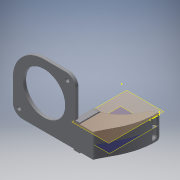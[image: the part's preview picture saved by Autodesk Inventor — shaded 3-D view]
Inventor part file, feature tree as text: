
AUTODESK INVENTOR PART (.ipt)
format: ipt  version: 2016 (Build 200138000, 138)  size: 1,453,568 bytes
history: native  units: mm
features: projected_geometry x29, sketch x27, extrude x24, fillet x11, reference x5, plane x2, chamfer x2, shell x1, imported_body x1, boolean_combine x1
ambient origin geometry x8: Origin, YZ Plane, XZ Plane, XY Plane, X Axis, Y Axis, Z Axis, Center Point
bodies: Solid1 (feature_tree), Solid2 (feature_tree)
feature tree (103):
  plane  "Work Plane1"
  extrude  "Extrusion1"  Depth=25.0mm TaperAngle=45.0deg
  chamfer  "Chamfer1"  Distance=2.0mm
  sketch  "Sketch2"  dims[d5=2.0mm]
  shell  "Shell1"  Thickness=3.0mm
  extrude  "Extrusion2"  Depth=2.0mm
  sketch  "Sketch4"  dims[d10=5.5mm d11=2.0mm d12=17.25mm d13=4.0mm d14=16.0mm d15=0.0mm d21=1.0mm d22=0.0mm]
  sketch  "Sketch5"  dims[d23=11.0mm d24=1.0mm d25=45.0deg d26=0.5mm d27=0.0mm]
  fillet  "Fillet1"  Radius=17.25mm
  fillet  "Fillet2"  Radius=4.0mm
  fillet  "Fillet3"  Radius=16.0mm
  fillet  "Fillet4"  Radius=1.0mm
  fillet  "Fillet5"  Radius=0.5mm
  extrude  "Extrusion3"  Depth=3.0mm TaperAngle=0.0deg
  extrude  "Extrusion5"  Depth=4.0mm TaperAngle=0.0deg
  chamfer  "Chamfer2"  Distance=3.0mm
  imported_body  "Base1"
  boolean_combine  "Combine1"
  extrude  "Extrusion6"  Depth=3.0mm TaperAngle=0.0deg
  extrude  "Extrusion7"  Depth=10.0mm
  extrude  "Extrusion8"  Depth=1.0mm TaperAngle=0.0deg
  extrude  "Extrusion9"  Depth=10.0mm
  extrude  "Extrusion10"  Depth=30.0mm
  extrude  "Extrusion11"  Depth=1.0mm TaperAngle=0.0deg
  extrude  "Extrusion12"  Depth=1.0mm TaperAngle=0.0deg
  fillet  "Fillet7"  Radius=0.5mm
  fillet  "Fillet8"  Radius=20.0mm
  fillet  "Fillet11"  Radius=0.1mm
  extrude  "Extrusion13"  Depth=20.0mm TaperAngle=0.0deg
  extrude  "Extrusion14"  Depth=6.0mm
  fillet  "Fillet12"  Radius=8.5mm
  extrude  "Extrusion15"  Depth=0.1mm
  fillet  "Fillet13"  [1 undecoded]
  plane  "Work Plane2"
  extrude  "Extrusion16"  [1 undecoded]
  extrude  "Extrusion17"  [1 undecoded]
  extrude  "Extrusion18"  [1 undecoded]
  extrude  "Extrusion19"  [1 undecoded]
  extrude  "Extrusion20"  [1 undecoded]
  extrude  "Extrusion21"  [1 undecoded]
  extrude  "Extrusion22"  [1 undecoded]
  extrude  "Extrusion23"  [1 undecoded]
  extrude  "Extrusion24"  [1 undecoded]
  extrude  "Extrusion25"  [1 undecoded]
  fillet  "Fillet14"  [1 undecoded]
  sketch  "Sketch1"  dims[d0=20.0mm d1=0.0mm d2=25.0mm d3=13.0mm d4=45.0deg]
  sketch  "Sketch3"  dims[d6=8.0mm d7=2.0mm d8=0.0mm d9=3.0mm]
  reference  "Reference1"
  projected_geometry  "Projected Loop1"
  sketch  "Sketch6"  dims[d28=1.0mm d29=3.0mm d30=0.0mm]
  reference  "Reference2"
  reference  "Reference3"
  reference  "Reference4"
  reference  "Reference5"
  sketch  "Sketch8"  dims[d31=4.0mm d32=0.0mm d33=4.0mm d34=0.0mm d36=3.0mm d37=0.0mm]
  projected_geometry  "Projected Loop2"
  sketch  "Sketch9"  dims[d38=3.0mm d39=0.0mm d40=3.0mm d41=0.0mm]
  projected_geometry  "Projected Loop3"
  projected_geometry  "Projected Loop4"
  sketch  "Sketch10"  dims[d42=1.5mm d43=10.0mm]
  projected_geometry  "Projected Loop5"
  projected_geometry  "Projected Loop6"
  sketch  "Sketch11"  dims[d46=3.0mm d47=1.0mm d48=0.0mm]
  projected_geometry  "Projected Loop7"
  sketch  "Sketch12"  dims[d49=20.0mm d50=0.0mm d51=10.0mm]
  projected_geometry  "Projected Loop8"
  sketch  "Sketch13"  dims[d52=20.0mm d53=0.0mm d54=30.0mm]
  projected_geometry  "Projected Loop9"
  sketch  "Sketch14"  dims[d55=7.5mm d56=1.0mm d57=0.0mm]
  projected_geometry  "Projected Loop10"
  projected_geometry  "Projected Loop11"
  projected_geometry  "Projected Loop12"
  sketch  "Sketch15"  dims[d58=1.0mm d59=0.0mm d60=1.0mm d61=0.0mm d62=0.5mm d63=0.0mm d64=20.0mm d65=0.0mm d66=0.1mm d67=0.0mm]
  projected_geometry  "Projected Loop13"
  sketch  "Sketch16"  dims[d68=0.1mm d69=0.0mm d70=20.0mm d71=0.0mm]
  projected_geometry  "Projected Loop14"
  projected_geometry  "Projected Loop15"
  sketch  "Sketch17"  dims[d72=12.566371mm d73=6.0mm d74=8.5mm d75=0.0mm]
  projected_geometry  "Projected Loop16"
  sketch  "Sketch18"  dims[d76=8.5mm d77=0.0mm d78=0.1mm]
  projected_geometry  "Projected Loop17"
  sketch  "Sketch19"
  sketch  "Sketch20"
  projected_geometry  "Projected Loop18"
  projected_geometry  "Projected Loop19"
  sketch  "Sketch21"
  projected_geometry  "Projected Loop20"
  projected_geometry  "Projected Loop21"
  sketch  "Sketch22"
  projected_geometry  "Projected Loop22"
  sketch  "Sketch23"
  projected_geometry  "Projected Loop23"
  sketch  "Sketch24"
  projected_geometry  "Projected Loop24"
  sketch  "Sketch25"
  projected_geometry  "Projected Loop25"
  sketch  "Sketch26"
  projected_geometry  "Projected Loop26"
  sketch  "Sketch27"
  projected_geometry  "Projected Loop27"
  sketch  "Sketch28"
  projected_geometry  "Projected Loop28"
  projected_geometry  "Project Cut Edges1"
note: 12 required parameter values undecoded (feature->parameter linkage not recoverable at this tier; creation-order binding heuristic only, values carry confidence <= 0.55)
